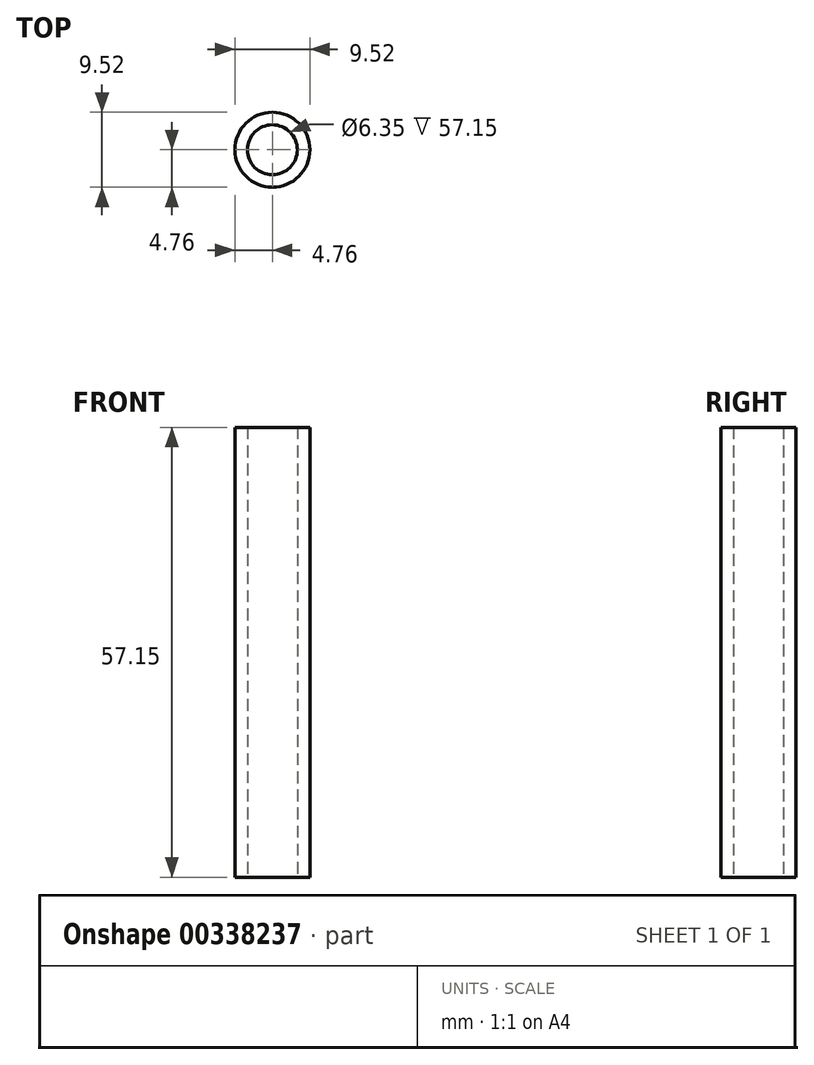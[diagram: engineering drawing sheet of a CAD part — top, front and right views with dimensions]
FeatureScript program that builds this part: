
annotation { "Feature Type Name" : "Feature", "Feature Type Description" : "" }
export const myFeature = defineFeature(function(context is Context, id is Id, definition is map)
    precondition{}
    {
        {
            var Q0;
            Q0=qCreatedBy(makeId("Top.planeOp"),FACE);
            var sketch = newSketch(context, id + "F0", { "sketchPlane" : qUnion([Q0])});
            skCircle(sketch, "E0", {"center": v(0, 0) * mm, "radius": 3.18 * mm});
            skCircle(sketch, "E1", {"center": v(0, 0) * mm, "radius": 4.76 * mm});
            skSolve(sketch);
        }
        {
            var Q0;
            Q0=qSketchRegion(id+"F0",true);
            extrude(context, id + "F1", {"entities" : qUnion([Q0]), "depth" : 57.15 * mm});
        }
    });
